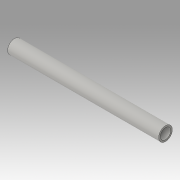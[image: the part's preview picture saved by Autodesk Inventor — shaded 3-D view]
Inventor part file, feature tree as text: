
AUTODESK INVENTOR PART (.ipt)
format: ipt  version: 2016 (Build 200138000, 138)  size: 77,312 bytes
history: native  units: in
note: dims shown in document units (in); Inventor stores cm internally (conversion verified against a paired STEP export)
features: extrude x1, sketch x1
ambient origin geometry x8: Origin, YZ Plane, XZ Plane, XY Plane, X Axis, Y Axis, Z Axis, Center Point
bodies: Solid1 (feature_tree)
feature tree (2):
  extrude  "Extrusion1"  Depth=6.953in
  sketch  "Sketch1"  dims[d0=0.635in d1=0.48in d2=6.953in d3=0.0in]
